# Revit family: Pole-PC2_Rakks
name_source: partatom
category: Specialty Equipment
units: mm (PartAtom-declared; Revit-internal decimal feet)

## family parameters
Always vertical = Yes
Classification Number = 23.40.50.31.11.14
Cut with Voids When Loaded = No
Enable Cutting in Views = No
Maintain Annotation Orientation = No
Part Type = Normal
Room Calculation Point = No
Round Connector Dimension = Use Diameter
Shared = Yes
Work Plane-Based = No

## types (7) — shared parameters
Assembly Code = E1010500
Capacity (Weight) = 0.00 lb
Construction Details = http://www.arcat.com
Default Elevation = 0' - 0"
Green Building-LEED = http://www.arcat.com
Installation-Fabrication = http://www.rakks.com
Keynote = 10 56 00
Manufacturer = Rangine Corp. - Rakks
Manufacturer Fax = 781-455-8702
Manufacturer Website = http://www.rakks.com
Material = Metal - Clear Anodized
Product Data = http://www.arcat.com
Product Properties = http://www.arcat.com
Revision = R1_03-2010
Sales Information = http://store.rakks.com
Send Message = http://www.arcat.com
Specification = http://www.arcat.com
Test Data = http://www.rakks.com
URL = http://www.rakks.com
zero-valued in all types: Expected Lifespan (Years), Maintenance Schedule (Months), Warranty Duration (Years)

## per-type parameters (varying)
| type | Return to Wall |
| A Mount | No |
| B Mount | No |
| C Mount | No |
| D Mount | No |
| E Mount | No |
| F Mount | Yes |
| G Mount | Yes |

## geometry (parser evidence)
native form markers: Blend x6, Sweep x3
no freeform markers — native parametric forms only
